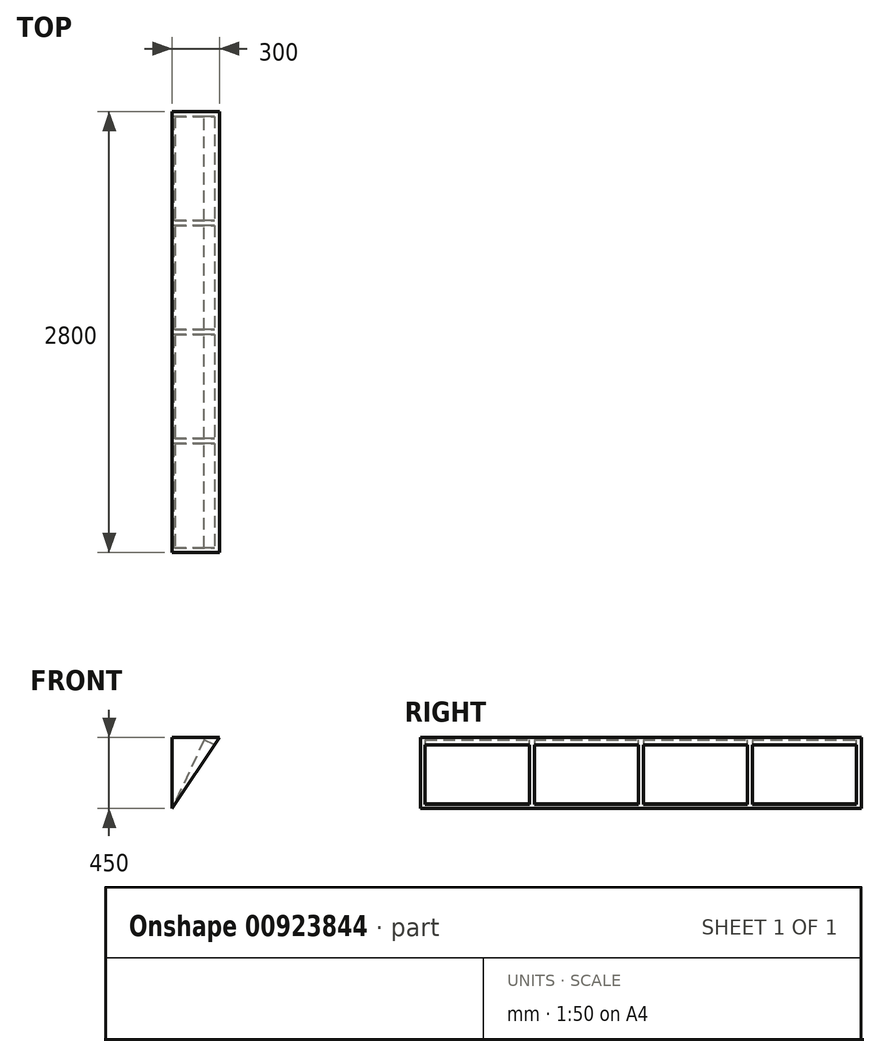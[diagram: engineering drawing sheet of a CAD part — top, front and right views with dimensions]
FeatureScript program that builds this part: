
annotation { "Feature Type Name" : "Feature", "Feature Type Description" : "" }
export const myFeature = defineFeature(function(context is Context, id is Id, definition is map)
    precondition{}
    {
        {
            var Q0;
            Q0=qCreatedBy(makeId("Front.planeOp"),FACE);
            var sketch = newSketch(context, id + "F0", { "sketchPlane" : qUnion([Q0])});
            skLineSegment(sketch, "E0", {"start": v(0, 0) * mm, "end": v(300, 0) * mm});
            skLineSegment(sketch, "E1", {"start": v(300, 0) * mm, "end": v(0, -450) * mm});
            skLineSegment(sketch, "E2", {"start": v(0, -450) * mm, "end": v(0, 0) * mm});
            skSolve(sketch);
        }
        {
            var Q0;
            Q0=makeQuery(id+"F0.imprint","IMPRINT",FACE,{"disambiguationData":[TD([[makeQuery(id+"F0.imprint","IMPRINT",EDGE,{"derivedFrom":sQuery(id+"F0.wireOp",EDGE,"E0")}),-1.0]])]});
            extrude(context, id + "F1", {"entities" : qUnion([Q0]), "depth" : 2800 * mm, "offsetDistance" : 25 * mm});
        }
        {
            var Q0;
            Q0=makeQuery(id+"F1.opExtrude","SWEPT_EDGE",EDGE,{"disambiguationData":[OSD([sQuery(id+"F0.wireOp",EDGE,"E1"),sQuery(id+"F0.wireOp",EDGE,"E2")])]});
            cPlane(context, id + "F2", {"entities" : qUnion([Q0]), "cplaneType" : CPlaneType.LINE_ANGLE, "offset" : 25 * mm, "angle" : 65 * degree, "oppositeDirection" : true, "width" : 150 * mm, "height" : 150 * mm});
        }
        {
            var Q0;
            Q0=qCreatedBy(id+"F2.planeOp",FACE);
            var sketch = newSketch(context, id + "F3", { "sketchPlane" : qUnion([Q0])});
            skLineSegment(sketch, "E3.bottom", {"start": v(2770, 72.16) * mm, "end": v(2107.5, 72.16) * mm});
            skLineSegment(sketch, "E3.top", {"start": v(2770, -377.84) * mm, "end": v(2107.5, -377.84) * mm});
            skLineSegment(sketch, "E3.left", {"start": v(2770, 72.16) * mm, "end": v(2770, -377.84) * mm});
            skLineSegment(sketch, "E3.right", {"start": v(2107.5, 72.16) * mm, "end": v(2107.5, -377.84) * mm});
            skLineSegment(sketch, "E4.1.0.0", {"start": v(2077.5, 72.16) * mm, "end": v(1415, 72.16) * mm});
            skLineSegment(sketch, "E4.1.0.1", {"start": v(2077.5, 72.16) * mm, "end": v(2077.5, -377.84) * mm});
            skLineSegment(sketch, "E4.1.0.2", {"start": v(2077.5, -377.84) * mm, "end": v(1415, -377.84) * mm});
            skLineSegment(sketch, "E4.1.0.3", {"start": v(1415, 72.16) * mm, "end": v(1415, -377.84) * mm});
            skLineSegment(sketch, "E4.2.0.0", {"start": v(1385, 72.16) * mm, "end": v(722.5, 72.16) * mm});
            skLineSegment(sketch, "E4.2.0.1", {"start": v(1385, 72.16) * mm, "end": v(1385, -377.84) * mm});
            skLineSegment(sketch, "E4.2.0.2", {"start": v(1385, -377.84) * mm, "end": v(722.5, -377.84) * mm});
            skLineSegment(sketch, "E4.2.0.3", {"start": v(722.5, 72.16) * mm, "end": v(722.5, -377.84) * mm});
            skLineSegment(sketch, "E4.3.0.0", {"start": v(692.5, 72.16) * mm, "end": v(30, 72.16) * mm});
            skLineSegment(sketch, "E4.3.0.1", {"start": v(692.5, 72.16) * mm, "end": v(692.5, -377.84) * mm});
            skLineSegment(sketch, "E4.3.0.2", {"start": v(692.5, -377.84) * mm, "end": v(30, -377.84) * mm});
            skLineSegment(sketch, "E4.3.0.3", {"start": v(30, 72.16) * mm, "end": v(30, -377.84) * mm});
            skLineSegment(sketch, "E4.direction1", {"start": v(2115, 72.16) * mm, "end": v(1422.5, 72.16) * mm, "construction": true});
            skSolve(sketch);
        }
        {
            var Q0;
            Q0 = qSketchRegion(id + "F3", true);
            extrude(context, id + "F4", {"entities" : qUnion([Q0]), "operationType" : NewBodyOperationType.REMOVE, "oppositeDirection" : true, "depth" : 247 * mm, "offsetDistance" : 25 * mm});
        }
    });
